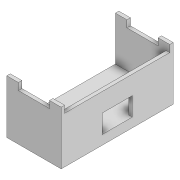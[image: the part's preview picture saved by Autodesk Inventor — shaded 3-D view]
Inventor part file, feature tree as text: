
AUTODESK INVENTOR PART (.ipt)
format: ipt  version: 2021 (Build 250183000, 183)  size: 143,360 bytes
history: native  units: in
note: dims shown in document units (in); Inventor stores cm internally (conversion verified against a paired STEP export)
features: extrude x5, sketch x4
ambient origin geometry x8: Origin, YZ Plane, XZ Plane, XY Plane, X Axis, Y Axis, Z Axis, Center Point
bodies: Solid1 (feature_tree)
feature tree (9):
  sketch  "Sketch1"  dims[d0=1.7795in d1=0.8031in]
  extrude  "Extrusion1"  Depth=1.7795in
  extrude  "Extrusion2"  Depth=0.7874in TaperAngle=0.0deg
  extrude  "Extrusion3"  Depth=0.1969in
  extrude  "Extrusion4"  Depth=0.693in
  extrude  "Extrusion5"  Depth=0.6928in
  sketch  "Sketch2"  dims[d2=0.0591in d3=0.7874in d4=0.0in]
  sketch  "Sketch3"  dims[d5=0.3937in d6=0.1969in]
  sketch  "Sketch4"  dims[d7=0.0591in d8=0.693in d9=0.6928in d10=0.315in d11=0.2362in d12=0.0in d13=0.1575in d14=0.0in d15=0.6299in d16=0.0in d17=0.0in d18=0.1969in d19=0.1969in d20=0.1969in d21=0.1969in d22=0.1181in d23=0.0in]
